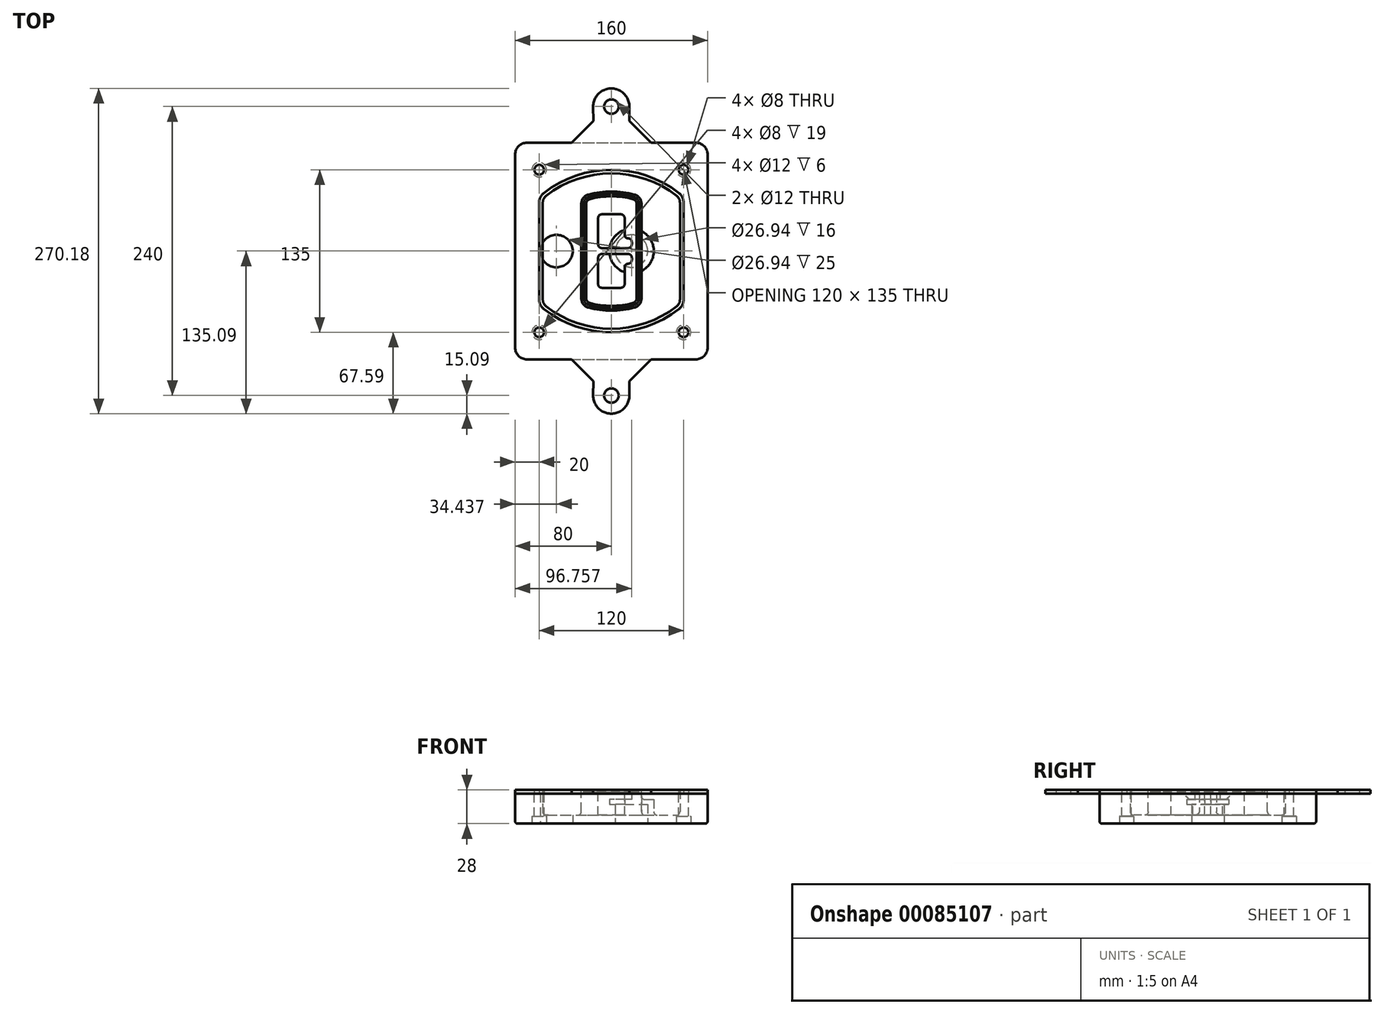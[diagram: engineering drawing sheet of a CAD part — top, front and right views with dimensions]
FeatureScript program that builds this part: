
annotation { "Feature Type Name" : "Feature", "Feature Type Description" : "" }
export const myFeature = defineFeature(function(context is Context, id is Id, definition is map)
    precondition{}
    {
        {
            var Q0;
            Q0=qCreatedBy(makeId("Top.planeOp"),FACE);
            var sketch = newSketch(context, id + "F0", { "sketchPlane" : qUnion([Q0])});
            skPoint(sketch, "E0.rect.middle", {"position": v(0, 0) * mm});
            skLineSegment(sketch, "E1.bottom", {"start": v(-70, -90) * mm, "end": v(70, -90) * mm});
            skLineSegment(sketch, "E1.top", {"start": v(-70, 90) * mm, "end": v(70, 90) * mm});
            skLineSegment(sketch, "E1.left", {"start": v(-80, -80) * mm, "end": v(-80, 80) * mm});
            skLineSegment(sketch, "E1.right", {"start": v(80, -80) * mm, "end": v(80, 80) * mm});
            skLineSegment(sketch, "E2", {"start": v(-80, 90) * mm, "end": v(80, -90) * mm, "construction": true});
            skLineSegment(sketch, "E3", {"start": v(80, 90) * mm, "end": v(-80, -90) * mm, "construction": true});
            skCircle(sketch, "E4", {"center": v(-60, 67.5) * mm, "radius": 4 * mm});
            skCircle(sketch, "E5", {"center": v(60, 67.5) * mm, "radius": 4 * mm});
            skCircle(sketch, "E6", {"center": v(60, -67.5) * mm, "radius": 4 * mm});
            skCircle(sketch, "E7", {"center": v(-60, -67.5) * mm, "radius": 4 * mm});
            skLineSegment(sketch, "E8", {"start": v(-60, 67.5) * mm, "end": v(60, 67.5) * mm, "construction": true});
            skLineSegment(sketch, "E9", {"start": v(60, 67.5) * mm, "end": v(60, -67.5) * mm, "construction": true});
            skLineSegment(sketch, "E10", {"start": v(60, -67.5) * mm, "end": v(-60, -67.5) * mm, "construction": true});
            skLineSegment(sketch, "E11", {"start": v(-60, -67.5) * mm, "end": v(-60, 67.5) * mm, "construction": true});
            skLineSegment(sketch, "E12", {"start": v(-60, 40.3) * mm, "end": v(-60, -40.3) * mm});
            skLineSegment(sketch, "E13", {"start": v(60, 40.3) * mm, "end": v(60, -40.3) * mm});
            skArc(sketch, "E14", {"start": v(56.15, 48.18) * mm, "mid": v(0, 67.5) * mm, "end": v(-56.15, 48.18) * mm});
            skArc(sketch, "E15", {"start": v(-56.15, -48.18) * mm, "mid": v(0, -67.5) * mm, "end": v(56.15, -48.18) * mm});
            skLineSegment(sketch, "E16", {"start": v(-60, 0) * mm, "end": v(60, 0) * mm, "construction": true});
            skPoint(sketch, "E17.visualSharp", {"position": v(-60, -45) * mm});
            skArc(sketch, "E17.filletArc", {"start": v(-60, -40.3) * mm, "mid": v(-58.99, -44.68) * mm, "end": v(-56.15, -48.18) * mm});
            skPoint(sketch, "E18.visualSharp", {"position": v(-60, 45) * mm});
            skArc(sketch, "E18.filletArc", {"start": v(-56.15, 48.18) * mm, "mid": v(-58.99, 44.68) * mm, "end": v(-60, 40.3) * mm});
            skPoint(sketch, "E19.visualSharp", {"position": v(60, 45) * mm});
            skArc(sketch, "E19.filletArc", {"start": v(60, 40.3) * mm, "mid": v(58.99, 44.68) * mm, "end": v(56.15, 48.18) * mm});
            skPoint(sketch, "E20.visualSharp", {"position": v(60, -45) * mm});
            skArc(sketch, "E20.filletArc", {"start": v(56.15, -48.18) * mm, "mid": v(58.99, -44.68) * mm, "end": v(60, -40.3) * mm});
            skPoint(sketch, "E21.visualSharp", {"position": v(-80, 90) * mm});
            skArc(sketch, "E21.filletArc", {"start": v(-70, 90) * mm, "mid": v(-77.07, 87.07) * mm, "end": v(-80, 80) * mm});
            skPoint(sketch, "E22.visualSharp", {"position": v(80, 90) * mm});
            skArc(sketch, "E22.filletArc", {"start": v(80, 80) * mm, "mid": v(77.07, 87.07) * mm, "end": v(70, 90) * mm});
            skPoint(sketch, "E23.visualSharp", {"position": v(80, -90) * mm});
            skArc(sketch, "E23.filletArc", {"start": v(70, -90) * mm, "mid": v(77.07, -87.07) * mm, "end": v(80, -80) * mm});
            skPoint(sketch, "E24.visualSharp", {"position": v(-80, -90) * mm});
            skArc(sketch, "E24.filletArc", {"start": v(-80, -80) * mm, "mid": v(-77.07, -87.07) * mm, "end": v(-70, -90) * mm});
            skArc(sketch, "E25.0", {"start": v(57, 40.3) * mm, "mid": v(56.3, 43.36) * mm, "end": v(54.3, 45.81) * mm});
            skLineSegment(sketch, "E25.1", {"start": v(57, 40.3) * mm, "end": v(57, -40.3) * mm});
            skArc(sketch, "E25.2", {"start": v(54.3, -45.81) * mm, "mid": v(56.3, -43.36) * mm, "end": v(57, -40.3) * mm});
            skArc(sketch, "E25.3", {"start": v(-54.3, -45.81) * mm, "mid": v(0, -64.5) * mm, "end": v(54.3, -45.81) * mm});
            skArc(sketch, "E25.4", {"start": v(-57, -40.3) * mm, "mid": v(-56.3, -43.36) * mm, "end": v(-54.3, -45.81) * mm});
            skArc(sketch, "E25.5", {"start": v(54.3, 45.81) * mm, "mid": v(0, 64.5) * mm, "end": v(-54.3, 45.81) * mm});
            skLineSegment(sketch, "E25.6", {"start": v(-57, 40.3) * mm, "end": v(-57, -40.3) * mm});
            skArc(sketch, "E25.7", {"start": v(-54.3, 45.81) * mm, "mid": v(-56.3, 43.36) * mm, "end": v(-57, 40.3) * mm});
            skArc(sketch, "E26.0", {"start": v(-58.62, 51.33) * mm, "mid": v(-62.58, 46.43) * mm, "end": v(-64, 40.3) * mm});
            skArc(sketch, "E26.1", {"start": v(58.62, 51.33) * mm, "mid": v(0, 71.5) * mm, "end": v(-58.62, 51.33) * mm});
            skArc(sketch, "E26.2", {"start": v(64, 40.3) * mm, "mid": v(62.58, 46.43) * mm, "end": v(58.62, 51.33) * mm});
            skLineSegment(sketch, "E26.3", {"start": v(64, 40.3) * mm, "end": v(64, -40.3) * mm});
            skArc(sketch, "E26.4", {"start": v(58.62, -51.33) * mm, "mid": v(62.58, -46.43) * mm, "end": v(64, -40.3) * mm});
            skLineSegment(sketch, "E26.5", {"start": v(-64, 40.3) * mm, "end": v(-64, -40.3) * mm});
            skArc(sketch, "E26.6", {"start": v(-58.62, -51.33) * mm, "mid": v(0, -71.5) * mm, "end": v(58.62, -51.33) * mm});
            skArc(sketch, "E26.7", {"start": v(-64, -40.3) * mm, "mid": v(-62.58, -46.43) * mm, "end": v(-58.62, -51.33) * mm});
            skSolve(sketch);
        }
        {
            var Q0;
            Q0=makeQuery(id+"F0.imprint","IMPRINT",FACE,{"disambiguationData":[TD([[makeQuery(id+"F0.imprint","IMPRINT",EDGE,{"derivedFrom":sQuery(id+"F0.wireOp",EDGE,"E1.bottom")}),1.0]])]});
            var Q1;
            Q1=makeQuery(id+"F0.imprint","IMPRINT",FACE,{"disambiguationData":[TD([[makeQuery(id+"F0.imprint","IMPRINT",EDGE,{"derivedFrom":sQuery(id+"F0.wireOp",EDGE,"E12")}),1.0]])]});
            var Q2;
            Q2=makeQuery(id+"F0.imprint","IMPRINT",FACE,{"disambiguationData":[TD([[makeQuery(id+"F0.imprint","IMPRINT",EDGE,{"derivedFrom":sQuery(id+"F0.wireOp",EDGE,"E25.0")}),1.0]])]});
            var Q3;
            Q3=makeQuery(id+"F0.imprint","IMPRINT",FACE,{"disambiguationData":[TD([[makeQuery(id+"F0.imprint","IMPRINT",EDGE,{"derivedFrom":sQuery(id+"F0.wireOp",EDGE,"E12")}),-1.0]])]});
            extrude(context, id + "F1", {"entities" : qUnion([Q0, Q1, Q2, Q3]), "oppositeDirection" : true, "depth" : 25 * mm});
        }
        {
            var Q0;
            Q0=makeQuery(id+"F0.imprint","IMPRINT",FACE,{"disambiguationData":[TD([[makeQuery(id+"F0.imprint","IMPRINT",EDGE,{"derivedFrom":sQuery(id+"F0.wireOp",EDGE,"E12")}),1.0]])]});
            extrude(context, id + "F2", {"entities" : qUnion([Q0]), "operationType" : NewBodyOperationType.ADD, "depth" : 3 * mm});
        }
        {
            var Q0;
            Q0=makeQuery(id+"F0.imprint","IMPRINT",FACE,{"disambiguationData":[TD([[makeQuery(id+"F0.imprint","IMPRINT",EDGE,{"derivedFrom":sQuery(id+"F0.wireOp",EDGE,"E25.0")}),1.0]])]});
            extrude(context, id + "F3", {"entities" : qUnion([Q0]), "operationType" : NewBodyOperationType.REMOVE, "oppositeDirection" : true, "depth" : 18 * mm});
        }
        {
            var Q0;
            Q0=makeQuery(id+"F2.opExtrude","CAP_FACE",FACE,{"disambiguationData":[OSD([sQuery(id+"F0.wireOp",EDGE,"E12"),sQuery(id+"F0.wireOp",EDGE,"E13"),sQuery(id+"F0.wireOp",EDGE,"E14"),sQuery(id+"F0.wireOp",EDGE,"E15"),sQuery(id+"F0.wireOp",EDGE,"E17.filletArc"),sQuery(id+"F0.wireOp",EDGE,"E18.filletArc"),sQuery(id+"F0.wireOp",EDGE,"E19.filletArc"),sQuery(id+"F0.wireOp",EDGE,"E20.filletArc"),sQuery(id+"F0.wireOp",EDGE,"E25.0"),sQuery(id+"F0.wireOp",EDGE,"E25.1"),sQuery(id+"F0.wireOp",EDGE,"E25.2"),sQuery(id+"F0.wireOp",EDGE,"E25.3"),sQuery(id+"F0.wireOp",EDGE,"E25.4"),sQuery(id+"F0.wireOp",EDGE,"E25.5"),sQuery(id+"F0.wireOp",EDGE,"E25.6"),sQuery(id+"F0.wireOp",EDGE,"E25.7")])],"isStart":false});
            var sketch = newSketch(context, id + "F4", { "sketchPlane" : qUnion([Q0])});
            skArc(sketch, "E27.0", {"start": v(-19.08, -46.97) * mm, "mid": v(0, -49.5) * mm, "end": v(19.08, -46.97) * mm});
            skArc(sketch, "E28.0", {"start": v(19.08, 46.97) * mm, "mid": v(0, 49.5) * mm, "end": v(-19.08, 46.97) * mm});
            skLineSegment(sketch, "E29", {"start": v(-25, 39.25) * mm, "end": v(-25, -39.25) * mm});
            skLineSegment(sketch, "E30", {"start": v(25, 39.25) * mm, "end": v(25, -39.25) * mm});
            skLineSegment(sketch, "E31", {"start": v(-25, 45.1) * mm, "end": v(25, 45.1) * mm, "construction": true});
            skLineSegment(sketch, "E32", {"start": v(-25, -45.1) * mm, "end": v(25, -45.1) * mm, "construction": true});
            skPoint(sketch, "E33.visualSharp", {"position": v(-25, 45.1) * mm});
            skArc(sketch, "E33.filletArc", {"start": v(-19.08, 46.97) * mm, "mid": v(-23.35, 44.11) * mm, "end": v(-25, 39.25) * mm});
            skPoint(sketch, "E34.visualSharp", {"position": v(25, 45.1) * mm});
            skArc(sketch, "E34.filletArc", {"start": v(25, 39.25) * mm, "mid": v(23.35, 44.11) * mm, "end": v(19.08, 46.97) * mm});
            skPoint(sketch, "E35.visualSharp", {"position": v(25, -45.1) * mm});
            skArc(sketch, "E35.filletArc", {"start": v(19.08, -46.97) * mm, "mid": v(23.35, -44.11) * mm, "end": v(25, -39.25) * mm});
            skPoint(sketch, "E36.visualSharp", {"position": v(-25, -45.1) * mm});
            skArc(sketch, "E36.filletArc", {"start": v(-25, -39.25) * mm, "mid": v(-23.35, -44.11) * mm, "end": v(-19.08, -46.97) * mm});
            skArc(sketch, "E37.0", {"start": v(54.3, 45.81) * mm, "mid": v(0, 64.5) * mm, "end": v(-54.3, 45.81) * mm});
            skArc(sketch, "E37.1", {"start": v(-54.3, 45.81) * mm, "mid": v(-56.3, 43.36) * mm, "end": v(-57, 40.3) * mm});
            skLineSegment(sketch, "E37.2", {"start": v(-57, 40.3) * mm, "end": v(-57, -40.3) * mm});
            skArc(sketch, "E37.3", {"start": v(-57, -40.3) * mm, "mid": v(-56.3, -43.36) * mm, "end": v(-54.3, -45.81) * mm});
            skArc(sketch, "E37.4", {"start": v(-54.3, -45.81) * mm, "mid": v(0, -64.5) * mm, "end": v(54.3, -45.81) * mm});
            skArc(sketch, "E37.5", {"start": v(54.3, -45.81) * mm, "mid": v(56.3, -43.36) * mm, "end": v(57, -40.3) * mm});
            skLineSegment(sketch, "E37.6", {"start": v(57, 40.3) * mm, "end": v(57, -40.3) * mm});
            skArc(sketch, "E37.7", {"start": v(57, 40.3) * mm, "mid": v(56.3, 43.36) * mm, "end": v(54.3, 45.81) * mm});
            skLineSegment(sketch, "E38.0", {"start": v(23, 39.25) * mm, "end": v(23, -39.25) * mm});
            skArc(sketch, "E38.1", {"start": v(18.56, -45.04) * mm, "mid": v(21.76, -42.9) * mm, "end": v(23, -39.25) * mm});
            skArc(sketch, "E38.2", {"start": v(-18.56, -45.04) * mm, "mid": v(0, -47.5) * mm, "end": v(18.56, -45.04) * mm});
            skArc(sketch, "E38.3", {"start": v(-23, -39.25) * mm, "mid": v(-21.76, -42.9) * mm, "end": v(-18.56, -45.04) * mm});
            skLineSegment(sketch, "E38.4", {"start": v(-23, 39.25) * mm, "end": v(-23, -39.25) * mm});
            skArc(sketch, "E38.5", {"start": v(23, 39.25) * mm, "mid": v(21.76, 42.9) * mm, "end": v(18.56, 45.04) * mm});
            skArc(sketch, "E38.6", {"start": v(-18.56, 45.04) * mm, "mid": v(-21.76, 42.9) * mm, "end": v(-23, 39.25) * mm});
            skArc(sketch, "E38.7", {"start": v(18.56, 45.04) * mm, "mid": v(0, 47.5) * mm, "end": v(-18.56, 45.04) * mm});
            skArc(sketch, "E39.0", {"start": v(21, 39.25) * mm, "mid": v(20.18, 41.68) * mm, "end": v(18.04, 43.1) * mm});
            skLineSegment(sketch, "E39.1", {"start": v(21, 39.25) * mm, "end": v(21, -39.25) * mm});
            skArc(sketch, "E39.2", {"start": v(18.04, -43.1) * mm, "mid": v(20.18, -41.68) * mm, "end": v(21, -39.25) * mm});
            skArc(sketch, "E39.3", {"start": v(-18.04, -43.1) * mm, "mid": v(0, -45.5) * mm, "end": v(18.04, -43.1) * mm});
            skArc(sketch, "E39.4", {"start": v(-21, -39.25) * mm, "mid": v(-20.18, -41.68) * mm, "end": v(-18.04, -43.1) * mm});
            skArc(sketch, "E39.5", {"start": v(18.04, 43.1) * mm, "mid": v(0, 45.5) * mm, "end": v(-18.04, 43.1) * mm});
            skLineSegment(sketch, "E39.6", {"start": v(-21, 39.25) * mm, "end": v(-21, -39.25) * mm});
            skArc(sketch, "E39.7", {"start": v(-18.04, 43.1) * mm, "mid": v(-20.18, 41.68) * mm, "end": v(-21, 39.25) * mm});
            skLineSegment(sketch, "E40", {"start": v(-25, 0) * mm, "end": v(25, 0) * mm, "construction": true});
            skLineSegment(sketch, "E41", {"start": v(-11, 5.5) * mm, "end": v(-11, 27.5) * mm});
            skLineSegment(sketch, "E42", {"start": v(-8, 30.5) * mm, "end": v(8, 30.5) * mm});
            skLineSegment(sketch, "E43", {"start": v(11, 27.5) * mm, "end": v(11, 13.5) * mm});
            skLineSegment(sketch, "E44", {"start": v(14, 10.5) * mm, "end": v(14, 10.5) * mm});
            skLineSegment(sketch, "E45", {"start": v(17, 7.5) * mm, "end": v(17, 5.5) * mm});
            skLineSegment(sketch, "E46", {"start": v(14, 2.5) * mm, "end": v(-8, 2.5) * mm});
            skPoint(sketch, "E47.visualSharp", {"position": v(-11, 30.5) * mm});
            skArc(sketch, "E47.filletArc", {"start": v(-8, 30.5) * mm, "mid": v(-10.12, 29.62) * mm, "end": v(-11, 27.5) * mm});
            skPoint(sketch, "E48.visualSharp", {"position": v(11, 30.5) * mm});
            skArc(sketch, "E48.filletArc", {"start": v(11, 27.5) * mm, "mid": v(10.12, 29.62) * mm, "end": v(8, 30.5) * mm});
            skPoint(sketch, "E49.visualSharp", {"position": v(11, 10.5) * mm});
            skArc(sketch, "E49.filletArc", {"start": v(11, 13.5) * mm, "mid": v(11.88, 11.38) * mm, "end": v(14, 10.5) * mm});
            skPoint(sketch, "E50.visualSharp", {"position": v(17, 10.5) * mm});
            skArc(sketch, "E50.filletArc", {"start": v(17, 7.5) * mm, "mid": v(16.12, 9.62) * mm, "end": v(14, 10.5) * mm});
            skPoint(sketch, "E51.visualSharp", {"position": v(17, 2.5) * mm});
            skArc(sketch, "E51.filletArc", {"start": v(14, 2.5) * mm, "mid": v(16.12, 3.38) * mm, "end": v(17, 5.5) * mm});
            skPoint(sketch, "E52.visualSharp", {"position": v(-11, 2.5) * mm});
            skArc(sketch, "E52.filletArc", {"start": v(-11, 5.5) * mm, "mid": v(-10.12, 3.38) * mm, "end": v(-8, 2.5) * mm});
            skLineSegment(sketch, "E53.0.MirrorCS", {"start": v(14, -2.5) * mm, "end": v(-8, -2.5) * mm});
            skArc(sketch, "E54.0.MirrorCS", {"start": v(-11, -5.5) * mm, "mid": v(-10.12, -3.38) * mm, "end": v(-8, -2.5) * mm});
            skLineSegment(sketch, "E55.0.MirrorCS", {"start": v(-11, -5.5) * mm, "end": v(-11, -27.5) * mm});
            skArc(sketch, "E56.0.MirrorCS", {"start": v(-8, -30.5) * mm, "mid": v(-10.12, -29.62) * mm, "end": v(-11, -27.5) * mm});
            skLineSegment(sketch, "E57.0.MirrorCS", {"start": v(-8, -30.5) * mm, "end": v(8, -30.5) * mm});
            skArc(sketch, "E58.0.MirrorCS", {"start": v(11, -27.5) * mm, "mid": v(10.12, -29.62) * mm, "end": v(8, -30.5) * mm});
            skLineSegment(sketch, "E59.0.MirrorCS", {"start": v(11, -27.5) * mm, "end": v(11, -13.5) * mm});
            skArc(sketch, "E60.0.MirrorCS", {"start": v(11, -13.5) * mm, "mid": v(11.88, -11.38) * mm, "end": v(14, -10.5) * mm});
            skArc(sketch, "E61.0.MirrorCS", {"start": v(17, -7.5) * mm, "mid": v(16.12, -9.62) * mm, "end": v(14, -10.5) * mm});
            skLineSegment(sketch, "E62.0.MirrorCS", {"start": v(17, -7.5) * mm, "end": v(17, -5.5) * mm});
            skArc(sketch, "E63.0.MirrorCS", {"start": v(14, -2.5) * mm, "mid": v(16.12, -3.38) * mm, "end": v(17, -5.5) * mm});
            skSolve(sketch);
        }
        {
            var Q0;
            Q0=makeQuery(id+"F4.imprint","IMPRINT",FACE,{"disambiguationData":[TD([[makeQuery(id+"F4.imprint","IMPRINT",EDGE,{"derivedFrom":sQuery(id+"F4.wireOp",EDGE,"E27.0")}),1.0]])]});
            var Q1;
            Q1=makeQuery(id+"F4.imprint","IMPRINT",FACE,{"disambiguationData":[TD([[makeQuery(id+"F4.imprint","IMPRINT",EDGE,{"derivedFrom":sQuery(id+"F4.wireOp",EDGE,"E38.0")}),-1.0]])]});
            var Q2;
            Q2=makeQuery(id+"F4.imprint","IMPRINT",FACE,{"disambiguationData":[TD([[makeQuery(id+"F4.imprint","IMPRINT",EDGE,{"derivedFrom":sQuery(id+"F4.wireOp",EDGE,"E39.0")}),1.0]])]});
            extrude(context, id + "F5", {"entities" : qUnion([Q0, Q1, Q2]), "operationType" : NewBodyOperationType.ADD, "endBound" : BoundingType.UP_TO_NEXT, "oppositeDirection" : true, "depth" : 25 * mm});
        }
        {
            var Q0;
            Q0=makeQuery(id+"F4.imprint","IMPRINT",FACE,{"disambiguationData":[TD([[makeQuery(id+"F4.imprint","IMPRINT",EDGE,{"derivedFrom":sQuery(id+"F4.wireOp",EDGE,"E38.0")}),-1.0]])]});
            extrude(context, id + "F6", {"entities" : qUnion([Q0]), "operationType" : NewBodyOperationType.REMOVE, "oppositeDirection" : true, "depth" : 2 * mm});
        }
        {
            var Q0;
            Q0=makeQuery(id+"F1.opExtrude","CAP_FACE",FACE,{"disambiguationData":[OSD([sQuery(id+"F0.wireOp",EDGE,"E1.bottom"),sQuery(id+"F0.wireOp",EDGE,"E1.top"),sQuery(id+"F0.wireOp",EDGE,"E1.left"),sQuery(id+"F0.wireOp",EDGE,"E1.right"),sQuery(id+"F0.wireOp",EDGE,"E4"),sQuery(id+"F0.wireOp",EDGE,"E5"),sQuery(id+"F0.wireOp",EDGE,"E6"),sQuery(id+"F0.wireOp",EDGE,"E7"),sQuery(id+"F0.wireOp",EDGE,"E21.filletArc"),sQuery(id+"F0.wireOp",EDGE,"E22.filletArc"),sQuery(id+"F0.wireOp",EDGE,"E23.filletArc"),sQuery(id+"F0.wireOp",EDGE,"E24.filletArc")])],"isStart":false});
            var sketch = newSketch(context, id + "F7", { "sketchPlane" : qUnion([Q0])});
            skCircle(sketch, "E64", {"center": v(16.76, 0) * mm, "radius": 13.47 * mm});
            skCircle(sketch, "E65", {"center": v(-45.56, 0) * mm, "radius": 13.47 * mm});
            skLineSegment(sketch, "E66", {"start": v(80, 0) * mm, "end": v(-80, 0) * mm});
            skCircle(sketch, "E67", {"center": v(16.76, 0) * mm, "radius": 18.47 * mm});
            skCircle(sketch, "E68", {"center": v(60, -67.5) * mm, "radius": 6 * mm});
            skCircle(sketch, "E69", {"center": v(-60, -67.5) * mm, "radius": 6 * mm});
            skCircle(sketch, "E70", {"center": v(-60, 67.5) * mm, "radius": 6 * mm});
            skCircle(sketch, "E71", {"center": v(60, 67.5) * mm, "radius": 6 * mm});
            skSolve(sketch);
        }
        {
            var Q0;
            {var subQ1=sQuery(id+"F7.wireOp",EDGE,"E66");var subQ4=sQuery(id+"F7.wireOp",EDGE,"E64");var subQ6=makeQuery(id+"F7.imprint","INTERSECT",VERTEX,{"disambiguationData":[OD(0.0)],"derivedFrom":[subQ4,subQ1]});Q0=makeQuery(id+"F7.imprint","IMPRINT",FACE,{"disambiguationData":[TD([[makeQuery(id+"F7.imprint","IMPRINT",EDGE,{"disambiguationData":[TD([[subQ6,-1.0]])],"derivedFrom":subQ4}),-1.0]])]});}
            var Q1;
            {var subQ0=sQuery(id+"F7.wireOp",EDGE,"E66");var subQ1=sQuery(id+"F7.wireOp",EDGE,"E64");var subQ3=makeQuery(id+"F7.imprint","INTERSECT",VERTEX,{"disambiguationData":[OD(0.0)],"derivedFrom":[subQ1,subQ0]});Q1=makeQuery(id+"F7.imprint","IMPRINT",FACE,{"disambiguationData":[TD([[makeQuery(id+"F7.imprint","IMPRINT",EDGE,{"disambiguationData":[TD([[subQ3,-1.0]])],"derivedFrom":subQ1}),1.0]])]});}
            var Q2;
            {var subQ0=sQuery(id+"F7.wireOp",EDGE,"E66");var subQ1=sQuery(id+"F7.wireOp",EDGE,"E64");var subQ3=makeQuery(id+"F7.imprint","INTERSECT",VERTEX,{"disambiguationData":[OD(0.0)],"derivedFrom":[subQ1,subQ0]});Q2=makeQuery(id+"F7.imprint","IMPRINT",FACE,{"disambiguationData":[TD([[makeQuery(id+"F7.imprint","IMPRINT",EDGE,{"disambiguationData":[TD([[subQ3,1.0]])],"derivedFrom":subQ1}),1.0]])]});}
            var Q3;
            {var subQ1=sQuery(id+"F7.wireOp",EDGE,"E66");var subQ4=sQuery(id+"F7.wireOp",EDGE,"E64");var subQ6=makeQuery(id+"F7.imprint","INTERSECT",VERTEX,{"disambiguationData":[OD(0.0)],"derivedFrom":[subQ4,subQ1]});Q3=makeQuery(id+"F7.imprint","IMPRINT",FACE,{"disambiguationData":[TD([[makeQuery(id+"F7.imprint","IMPRINT",EDGE,{"disambiguationData":[TD([[subQ6,1.0]])],"derivedFrom":subQ4}),-1.0]])]});}
            extrude(context, id + "F8", {"entities" : qUnion([Q0, Q1, Q2, Q3]), "operationType" : NewBodyOperationType.ADD, "oppositeDirection" : true, "depth" : 20 * mm});
        }
        {
            var Q0;
            {var subQ0=sQuery(id+"F7.wireOp",EDGE,"E66");var subQ1=sQuery(id+"F7.wireOp",EDGE,"E64");var subQ3=makeQuery(id+"F7.imprint","INTERSECT",VERTEX,{"disambiguationData":[OD(0.0)],"derivedFrom":[subQ1,subQ0]});Q0=makeQuery(id+"F7.imprint","IMPRINT",FACE,{"disambiguationData":[TD([[makeQuery(id+"F7.imprint","IMPRINT",EDGE,{"disambiguationData":[TD([[subQ3,-1.0]])],"derivedFrom":subQ1}),1.0]])]});}
            var Q1;
            {var subQ0=sQuery(id+"F7.wireOp",EDGE,"E66");var subQ1=sQuery(id+"F7.wireOp",EDGE,"E64");var subQ3=makeQuery(id+"F7.imprint","INTERSECT",VERTEX,{"disambiguationData":[OD(0.0)],"derivedFrom":[subQ1,subQ0]});Q1=makeQuery(id+"F7.imprint","IMPRINT",FACE,{"disambiguationData":[TD([[makeQuery(id+"F7.imprint","IMPRINT",EDGE,{"disambiguationData":[TD([[subQ3,1.0]])],"derivedFrom":subQ1}),1.0]])]});}
            extrude(context, id + "F9", {"entities" : qUnion([Q0, Q1]), "operationType" : NewBodyOperationType.REMOVE, "oppositeDirection" : true, "depth" : 16 * mm});
        }
        {
            var Q0;
            {var subQ0=sQuery(id+"F7.wireOp",EDGE,"E66");var subQ1=sQuery(id+"F7.wireOp",EDGE,"E65");var subQ3=makeQuery(id+"F7.imprint","INTERSECT",VERTEX,{"disambiguationData":[OD(0.0)],"derivedFrom":[subQ1,subQ0]});Q0=makeQuery(id+"F7.imprint","IMPRINT",FACE,{"disambiguationData":[TD([[makeQuery(id+"F7.imprint","IMPRINT",EDGE,{"disambiguationData":[TD([[subQ3,-1.0]])],"derivedFrom":subQ1}),1.0]])]});}
            var Q1;
            {var subQ0=sQuery(id+"F7.wireOp",EDGE,"E66");var subQ1=sQuery(id+"F7.wireOp",EDGE,"E65");var subQ3=makeQuery(id+"F7.imprint","INTERSECT",VERTEX,{"disambiguationData":[OD(0.0)],"derivedFrom":[subQ1,subQ0]});Q1=makeQuery(id+"F7.imprint","IMPRINT",FACE,{"disambiguationData":[TD([[makeQuery(id+"F7.imprint","IMPRINT",EDGE,{"disambiguationData":[TD([[subQ3,1.0]])],"derivedFrom":subQ1}),1.0]])]});}
            extrude(context, id + "F10", {"entities" : qUnion([Q0, Q1]), "operationType" : NewBodyOperationType.REMOVE, "oppositeDirection" : true, "depth" : 25 * mm});
        }
        {
            var Q0;
            Q0=makeQuery(id+"F7.imprint","IMPRINT",FACE,{"disambiguationData":[TD([[makeQuery(id+"F7.imprint","IMPRINT",EDGE,{"derivedFrom":sQuery(id+"F7.wireOp",EDGE,"E68")}),1.0]])]});
            var Q1;
            Q1=makeQuery(id+"F7.imprint","IMPRINT",FACE,{"disambiguationData":[TD([[makeQuery(id+"F7.imprint","IMPRINT",EDGE,{"derivedFrom":makeQuery(id+"F1.opExtrude","CAP_EDGE",EDGE,{"disambiguationData":[OSD([sQuery(id+"F0.wireOp",EDGE,"E5")])],"isStart":false})}),-1.0]])]});
            var Q2;
            Q2=makeQuery(id+"F7.imprint","IMPRINT",FACE,{"disambiguationData":[TD([[makeQuery(id+"F7.imprint","IMPRINT",EDGE,{"derivedFrom":sQuery(id+"F7.wireOp",EDGE,"E69")}),1.0]])]});
            var Q3;
            Q3=makeQuery(id+"F7.imprint","IMPRINT",FACE,{"disambiguationData":[TD([[makeQuery(id+"F7.imprint","IMPRINT",EDGE,{"derivedFrom":makeQuery(id+"F1.opExtrude","CAP_EDGE",EDGE,{"disambiguationData":[OSD([sQuery(id+"F0.wireOp",EDGE,"E4")])],"isStart":false})}),-1.0]])]});
            var Q4;
            Q4=makeQuery(id+"F7.imprint","IMPRINT",FACE,{"disambiguationData":[TD([[makeQuery(id+"F7.imprint","IMPRINT",EDGE,{"derivedFrom":sQuery(id+"F7.wireOp",EDGE,"E70")}),1.0]])]});
            var Q5;
            Q5=makeQuery(id+"F7.imprint","IMPRINT",FACE,{"disambiguationData":[TD([[makeQuery(id+"F7.imprint","IMPRINT",EDGE,{"derivedFrom":makeQuery(id+"F1.opExtrude","CAP_EDGE",EDGE,{"disambiguationData":[OSD([sQuery(id+"F0.wireOp",EDGE,"E7")])],"isStart":false})}),-1.0]])]});
            var Q6;
            Q6=makeQuery(id+"F7.imprint","IMPRINT",FACE,{"disambiguationData":[TD([[makeQuery(id+"F7.imprint","IMPRINT",EDGE,{"derivedFrom":sQuery(id+"F7.wireOp",EDGE,"E71")}),1.0]])]});
            var Q7;
            Q7=makeQuery(id+"F7.imprint","IMPRINT",FACE,{"disambiguationData":[TD([[makeQuery(id+"F7.imprint","IMPRINT",EDGE,{"derivedFrom":makeQuery(id+"F1.opExtrude","CAP_EDGE",EDGE,{"disambiguationData":[OSD([sQuery(id+"F0.wireOp",EDGE,"E6")])],"isStart":false})}),-1.0]])]});
            extrude(context, id + "F11", {"entities" : qUnion([Q0, Q1, Q2, Q3, Q4, Q5, Q6, Q7]), "operationType" : NewBodyOperationType.REMOVE, "oppositeDirection" : true, "depth" : 6 * mm});
        }
        {
            var Q0;
            Q0=makeQuery(id+"F9.boolean.opBoolean","COPY",FACE,{"derivedFrom":makeQuery(id+"F9.opExtrude","CAP_FACE",FACE,{"disambiguationData":[OSD([sQuery(id+"F7.wireOp",EDGE,"E64")])],"isStart":false})});
            var sketch = newSketch(context, id + "F12", { "sketchPlane" : qUnion([Q0])});
            skArc(sketch, "E72.0", {"start": v(11, 17.55) * mm, "mid": v(2.57, 11.82) * mm, "end": v(-1.54, 2.5) * mm});
            skArc(sketch, "E72.1", {"start": v(-1.54, -2.5) * mm, "mid": v(2.57, -11.82) * mm, "end": v(11, -17.55) * mm});
            skLineSegment(sketch, "E73", {"start": v(-1.54, -2.5) * mm, "end": v(14, -2.5) * mm});
            skLineSegment(sketch, "E74.0", {"start": v(14, 2.5) * mm, "end": v(-1.54, 2.5) * mm});
            skArc(sketch, "E74.1", {"start": v(14, 2.5) * mm, "mid": v(16.12, 3.38) * mm, "end": v(17, 5.5) * mm});
            skLineSegment(sketch, "E74.2", {"start": v(17, 7.5) * mm, "end": v(17, 5.5) * mm});
            skArc(sketch, "E74.3", {"start": v(17, 7.5) * mm, "mid": v(16.12, 9.62) * mm, "end": v(14, 10.5) * mm});
            skArc(sketch, "E74.4", {"start": v(11, 13.5) * mm, "mid": v(11.88, 11.38) * mm, "end": v(14, 10.5) * mm});
            skLineSegment(sketch, "E74.5", {"start": v(11, 17.55) * mm, "end": v(11, 13.5) * mm});
            skLineSegment(sketch, "E74.7", {"start": v(14, -2.5) * mm, "end": v(-1.54, -2.5) * mm});
            skArc(sketch, "E74.8", {"start": v(14, -2.5) * mm, "mid": v(16.12, -3.38) * mm, "end": v(17, -5.5) * mm});
            skLineSegment(sketch, "E74.9", {"start": v(17, -7.5) * mm, "end": v(17, -5.5) * mm});
            skArc(sketch, "E74.10", {"start": v(17, -7.5) * mm, "mid": v(16.12, -9.62) * mm, "end": v(14, -10.5) * mm});
            skArc(sketch, "E74.11", {"start": v(11, -13.5) * mm, "mid": v(11.88, -11.38) * mm, "end": v(14, -10.5) * mm});
            skLineSegment(sketch, "E74.12", {"start": v(11, -17.55) * mm, "end": v(11, -13.5) * mm});
            skPoint(sketch, "E75.orphan", {"position": v(11, -27.5) * mm});
            skPoint(sketch, "E76.orphan", {"position": v(-8, -2.5) * mm});
            skPoint(sketch, "E77.orphan", {"position": v(-8, 2.5) * mm});
            skPoint(sketch, "E78.orphan", {"position": v(11, 27.5) * mm});
            skSolve(sketch);
        }
        {
            var Q0;
            {var subQ7=sQuery(id+"F12.wireOp",EDGE,"E72.0");var subQ14=sQuery(id+"F12.wireOp",EDGE,"E72.1");var subQ16=sQuery(id+"F12.wireOp",EDGE,"E74.1");var subQ18=sQuery(id+"F12.wireOp",EDGE,"E74.8");Q0=qUnion([makeQuery(id+"F12.imprint","IMPRINT",FACE,{"disambiguationData":[TD([[makeQuery(id+"F12.imprint","IMPRINT",EDGE,{"derivedFrom":subQ7}),1.0]])]}),makeQuery(id+"F12.imprint","IMPRINT",FACE,{"disambiguationData":[TD([[makeQuery(id+"F12.imprint","IMPRINT",EDGE,{"derivedFrom":subQ14}),1.0]])]}),makeQuery(id+"F12.imprint","IMPRINT",FACE,{"disambiguationData":[TD([[makeQuery(id+"F12.imprint","IMPRINT",EDGE,{"derivedFrom":subQ16}),1.0]])]}),makeQuery(id+"F12.imprint","IMPRINT",FACE,{"disambiguationData":[TD([[makeQuery(id+"F12.imprint","IMPRINT",EDGE,{"derivedFrom":subQ18}),-1.0]])]})]);}
            var Q1;
            Q1=makeQuery(id+"F5.boolean.opBoolean","SPLIT",FACE,{"disambiguationData":[TD([makeQuery(id+"F5.opExtrude","SWEPT_FACE",FACE,{"disambiguationData":[OSD([sQuery(id+"F4.wireOp",EDGE,"E41")])]})])],"derivedFrom":makeQuery(id+"F3.boolean.opBoolean","COPY",FACE,{"derivedFrom":makeQuery(id+"F3.opExtrude","CAP_FACE",FACE,{"disambiguationData":[OSD([sQuery(id+"F0.wireOp",EDGE,"E25.0"),sQuery(id+"F0.wireOp",EDGE,"E25.1"),sQuery(id+"F0.wireOp",EDGE,"E25.2"),sQuery(id+"F0.wireOp",EDGE,"E25.3"),sQuery(id+"F0.wireOp",EDGE,"E25.4"),sQuery(id+"F0.wireOp",EDGE,"E25.5"),sQuery(id+"F0.wireOp",EDGE,"E25.6"),sQuery(id+"F0.wireOp",EDGE,"E25.7")])],"isStart":false})})});
            extrude(context, id + "F13", {"entities" : qUnion([Q0]), "operationType" : NewBodyOperationType.REMOVE, "endBound" : BoundingType.UP_TO_SURFACE, "endBoundEntityFace" : qUnion([Q1]), "depth" : 25 * mm});
        }
        {
            var Q0;
            Q0=makeQuery(id+"F3.boolean.opBoolean","COPY",EDGE,{"derivedFrom":makeQuery(id+"F3.opExtrude","CAP_EDGE",EDGE,{"disambiguationData":[OSD([sQuery(id+"F0.wireOp",EDGE,"E25.6")])],"isStart":false})});
            var Q1;
            Q1=makeQuery(id+"F8.boolean.opBoolean","INTERSECT",EDGE,{"derivedFrom":[makeQuery(id+"F5.opExtrude","SWEPT_FACE",FACE,{"disambiguationData":[OSD([sQuery(id+"F4.wireOp",EDGE,"E30")])]}),makeQuery(id+"F8.opExtrude","CAP_FACE",FACE,{"disambiguationData":[OSD([sQuery(id+"F7.wireOp",EDGE,"E67")])],"isStart":false})]});
            var Q2;
            Q2=makeQuery(id+"F8.boolean.opBoolean","INTERSECT",EDGE,{"disambiguationData":[OD(1.0)],"derivedFrom":[makeQuery(id+"F5.opExtrude","SWEPT_FACE",FACE,{"disambiguationData":[OSD([sQuery(id+"F4.wireOp",EDGE,"E30")])]}),makeQuery(id+"F8.opExtrude","SWEPT_FACE",FACE,{"disambiguationData":[OSD([sQuery(id+"F7.wireOp",EDGE,"E67")])]})]});
            var Q3;
            {var subQ0=sQuery(id+"F4.wireOp",EDGE,"E30");Q3=makeQuery(id+"F8.boolean.opBoolean","SPLIT",EDGE,{"disambiguationData":[TD([makeQuery(id+"F5.opExtrude","SWEPT_FACE",FACE,{"disambiguationData":[OSD([sQuery(id+"F4.wireOp",EDGE,"E35.filletArc")])]})])],"derivedFrom":makeQuery(id+"F5.opExtrude","CAP_EDGE",EDGE,{"disambiguationData":[OSD([subQ0])],"isStart":false})});}
            var Q4;
            {var subQ0=sQuery(id+"F0.wireOp",EDGE,"E25.7");var subQ1=sQuery(id+"F0.wireOp",EDGE,"E25.1");var subQ2=sQuery(id+"F0.wireOp",EDGE,"E25.6");var subQ3=sQuery(id+"F0.wireOp",EDGE,"E25.5");var subQ4=sQuery(id+"F0.wireOp",EDGE,"E25.4");var subQ5=sQuery(id+"F0.wireOp",EDGE,"E25.0");var subQ6=sQuery(id+"F0.wireOp",EDGE,"E25.2");var subQ7=sQuery(id+"F0.wireOp",EDGE,"E25.3");Q4=makeQuery(id+"F8.boolean.opBoolean","INTERSECT",EDGE,{"derivedFrom":[makeQuery(id+"F5.boolean.opBoolean","SPLIT",FACE,{"disambiguationData":[TD([makeQuery(id+"F2.opExtrude","SWEPT_FACE",FACE,{"disambiguationData":[OSD([subQ5])]})])],"derivedFrom":makeQuery(id+"F3.boolean.opBoolean","COPY",FACE,{"derivedFrom":makeQuery(id+"F3.opExtrude","CAP_FACE",FACE,{"disambiguationData":[OSD([subQ5,subQ1,subQ6,subQ7,subQ4,subQ3,subQ2,subQ0])],"isStart":false})})}),makeQuery(id+"F8.opExtrude","SWEPT_FACE",FACE,{"disambiguationData":[OSD([sQuery(id+"F7.wireOp",EDGE,"E67")])]})]});}
            var Q5;
            Q5=makeQuery(id+"F8.boolean.opBoolean","INTERSECT",EDGE,{"disambiguationData":[OD(0.0)],"derivedFrom":[makeQuery(id+"F5.opExtrude","SWEPT_FACE",FACE,{"disambiguationData":[OSD([sQuery(id+"F4.wireOp",EDGE,"E30")])]}),makeQuery(id+"F8.opExtrude","SWEPT_FACE",FACE,{"disambiguationData":[OSD([sQuery(id+"F7.wireOp",EDGE,"E67")])]})]});
            fillet(context, id + "F14", {"entities" : qUnion([Q0, Q1, Q2, Q3, Q4, Q5]), "radius" : 3 * mm, "tangentPropagation" : true, "allowEdgeOverflow" : false});
        }
        {
            var Q0;
            Q0=makeQuery(id+"F1.opExtrude","CAP_EDGE",EDGE,{"disambiguationData":[OSD([sQuery(id+"F0.wireOp",EDGE,"E1.bottom")])],"isStart":false});
            fillet(context, id + "F15", {"entities" : qUnion([Q0]), "radius" : 2 * mm, "tangentPropagation" : true, "allowEdgeOverflow" : false});
        }
        {
            var Q0;
            {var subQ0=sQuery(id+"F0.wireOp",EDGE,"E22.filletArc");var subQ1=sQuery(id+"F0.wireOp",EDGE,"E7");var subQ2=sQuery(id+"F0.wireOp",EDGE,"E6");var subQ3=sQuery(id+"F0.wireOp",EDGE,"E5");var subQ4=sQuery(id+"F0.wireOp",EDGE,"E4");var subQ5=sQuery(id+"F0.wireOp",EDGE,"E1.bottom");var subQ6=sQuery(id+"F0.wireOp",EDGE,"E21.filletArc");var subQ7=sQuery(id+"F0.wireOp",EDGE,"E1.top");var subQ8=sQuery(id+"F0.wireOp",EDGE,"E1.left");var subQ9=sQuery(id+"F0.wireOp",EDGE,"E1.right");var subQ10=sQuery(id+"F0.wireOp",EDGE,"E23.filletArc");var subQ11=sQuery(id+"F0.wireOp",EDGE,"E24.filletArc");Q0=makeQuery(id+"F2.boolean.opBoolean","SPLIT",FACE,{"disambiguationData":[TD([makeQuery(id+"F1.opExtrude","SWEPT_FACE",FACE,{"disambiguationData":[OSD([subQ5])]})])],"derivedFrom":makeQuery(id+"F1.opExtrude","CAP_FACE",FACE,{"disambiguationData":[OSD([subQ5,subQ7,subQ8,subQ9,subQ4,subQ3,subQ2,subQ1,subQ6,subQ0,subQ10,subQ11])],"isStart":true})});}
            var sketch = newSketch(context, id + "F16", { "sketchPlane" : qUnion([Q0])});
            skLineSegment(sketch, "E79", {"start": v(0, 90) * mm, "end": v(0, 120) * mm, "construction": true});
            skCircle(sketch, "E80", {"center": v(0, 120) * mm, "radius": 6 * mm});
            skArc(sketch, "E81", {"start": v(14.9, 120) * mm, "mid": v(-0.1, 135.09) * mm, "end": v(-15.1, 120) * mm});
            skLineSegment(sketch, "E82", {"start": v(14.9, 120) * mm, "end": v(14.9, 108) * mm});
            skLineSegment(sketch, "E83", {"start": v(14.9, 108) * mm, "end": v(32.9, 90) * mm});
            skLineSegment(sketch, "E84", {"start": v(-15.1, 120) * mm, "end": v(-15.03, 108) * mm});
            skLineSegment(sketch, "E85", {"start": v(-15.03, 108) * mm, "end": v(-33.03, 90) * mm});
            skLineSegment(sketch, "E86", {"start": v(-80, 0) * mm, "end": v(80, 0) * mm, "construction": true});
            skLineSegment(sketch, "E87.MirrorCS", {"start": v(14.9, -108) * mm, "end": v(32.9, -90) * mm});
            skLineSegment(sketch, "E88.MirrorCS", {"start": v(-15.03, -108) * mm, "end": v(-33.03, -90) * mm});
            skArc(sketch, "E89.MirrorCS", {"start": v(14.9, -120) * mm, "mid": v(-0.1, -135.09) * mm, "end": v(-15.1, -120) * mm});
            skLineSegment(sketch, "E90.MirrorCS", {"start": v(14.9, -120) * mm, "end": v(14.9, -108) * mm});
            skLineSegment(sketch, "E91.MirrorCS", {"start": v(-15.1, -120) * mm, "end": v(-15.03, -108) * mm});
            skLineSegment(sketch, "E92.MirrorCS", {"start": v(0, -90) * mm, "end": v(0, -120) * mm, "construction": true});
            skCircle(sketch, "E93.MirrorC", {"center": v(0, -120) * mm, "radius": 6 * mm});
            skSolve(sketch);
        }
        {
            var Q0;
            Q0=makeQuery(id+"F16.imprint","IMPRINT",FACE,{"disambiguationData":[TD([[makeQuery(id+"F16.imprint","IMPRINT",EDGE,{"derivedFrom":makeQuery(id+"F1.opExtrude","CAP_EDGE",EDGE,{"disambiguationData":[OSD([sQuery(id+"F0.wireOp",EDGE,"E1.left")])],"isStart":true})}),-1.0]])]});
            var Q1;
            Q1=makeQuery(id+"F16.imprint","IMPRINT",FACE,{"disambiguationData":[TD([[makeQuery(id+"F16.imprint","IMPRINT",EDGE,{"derivedFrom":sQuery(id+"F16.wireOp",EDGE,"E80")}),-1.0]])]});
            var Q2;
            {var subQ0=sQuery(id+"F16.wireOp",EDGE,"E87.MirrorCS");Q2=makeQuery(id+"F16.imprint","IMPRINT",FACE,{"disambiguationData":[TD([[makeQuery(id+"F16.imprint","IMPRINT",EDGE,{"derivedFrom":subQ0}),1.0]])]});}
            var Q3;
            Q3=makeQuery(id+"F2.opExtrude","CAP_FACE",FACE,{"disambiguationData":[OSD([sQuery(id+"F0.wireOp",EDGE,"E12"),sQuery(id+"F0.wireOp",EDGE,"E13"),sQuery(id+"F0.wireOp",EDGE,"E14"),sQuery(id+"F0.wireOp",EDGE,"E15"),sQuery(id+"F0.wireOp",EDGE,"E17.filletArc"),sQuery(id+"F0.wireOp",EDGE,"E18.filletArc"),sQuery(id+"F0.wireOp",EDGE,"E19.filletArc"),sQuery(id+"F0.wireOp",EDGE,"E20.filletArc"),sQuery(id+"F0.wireOp",EDGE,"E25.0"),sQuery(id+"F0.wireOp",EDGE,"E25.1"),sQuery(id+"F0.wireOp",EDGE,"E25.2"),sQuery(id+"F0.wireOp",EDGE,"E25.3"),sQuery(id+"F0.wireOp",EDGE,"E25.4"),sQuery(id+"F0.wireOp",EDGE,"E25.5"),sQuery(id+"F0.wireOp",EDGE,"E25.6"),sQuery(id+"F0.wireOp",EDGE,"E25.7")])],"isStart":false});
            extrude(context, id + "F17", {"entities" : qUnion([Q0, Q1, Q2]), "endBound" : BoundingType.UP_TO_SURFACE, "endBoundEntityFace" : qUnion([Q3]), "depth" : 25 * mm});
        }
    });
